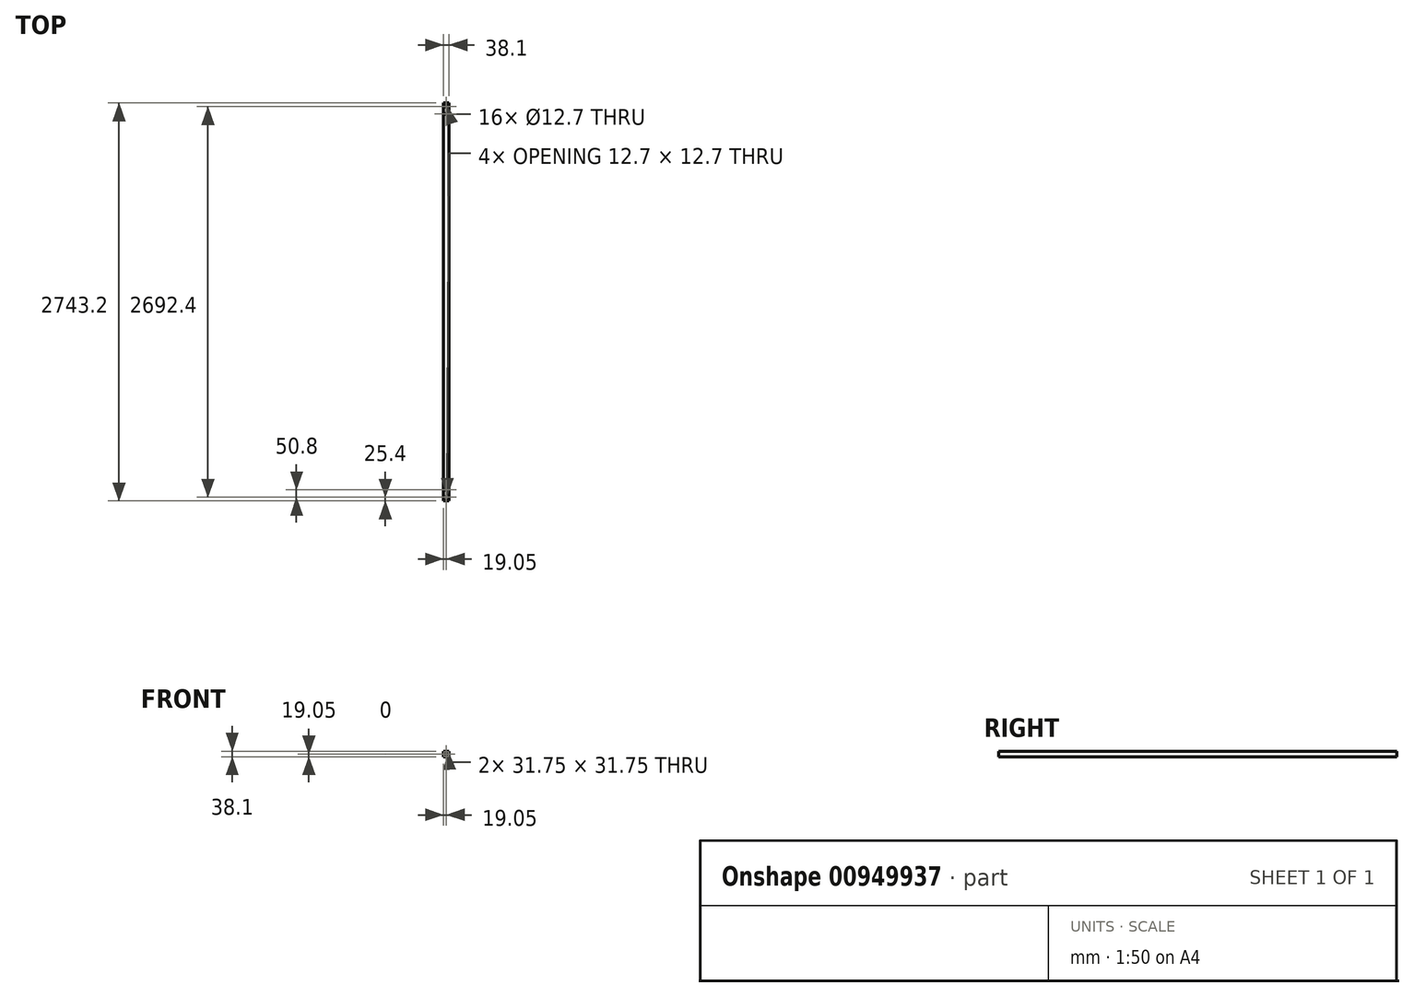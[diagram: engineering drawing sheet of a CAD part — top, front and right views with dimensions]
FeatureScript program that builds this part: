
annotation { "Feature Type Name" : "Feature", "Feature Type Description" : "" }
export const myFeature = defineFeature(function(context is Context, id is Id, definition is map)
    precondition{}
    {
        {
            var Q0;
            Q0=qCreatedBy(makeId("Front.planeOp"),FACE);
            var sketch = newSketch(context, id + "F0", { "sketchPlane" : qUnion([Q0])});
            skLineSegment(sketch, "E0.bottom", {"start": v(19.05, -19.05) * mm, "end": v(-19.05, -19.05) * mm});
            skLineSegment(sketch, "E0.top", {"start": v(19.05, 19.05) * mm, "end": v(-19.05, 19.05) * mm});
            skLineSegment(sketch, "E0.left", {"start": v(19.05, -19.05) * mm, "end": v(19.05, 19.05) * mm});
            skLineSegment(sketch, "E0.right", {"start": v(-19.05, -19.05) * mm, "end": v(-19.05, 19.05) * mm});
            skPoint(sketch, "E0.middle", {"position": v(0, 0) * mm});
            skLineSegment(sketch, "E1.bottom", {"start": v(15.88, -15.87) * mm, "end": v(-15.87, -15.88) * mm});
            skLineSegment(sketch, "E1.top", {"start": v(15.88, 15.88) * mm, "end": v(-15.88, 15.87) * mm});
            skLineSegment(sketch, "E1.left", {"start": v(15.88, -15.88) * mm, "end": v(15.88, 15.88) * mm});
            skLineSegment(sketch, "E1.right", {"start": v(-15.87, -15.88) * mm, "end": v(-15.88, 15.88) * mm});
            skSolve(sketch);
        }
        {
            var Q0;
            Q0 = qSketchRegion(id + "F0", true);
            var Q1;
            Q1 = qSketchRegion(id + "F2", true);
            extrude(context, id + "F1", {"entities" : qUnion([Q0, Q1]), "depth" : 2743.2 * mm, "offsetDistance" : 25.4 * mm});
        }
        {
            var Q0;
            Q0=makeQuery(id+"F1.opExtrude","SWEPT_FACE",FACE,{"disambiguationData":[OSD([sQuery(id+"F0.wireOp",EDGE,"E0.top")])]});
            var sketch = newSketch(context, id + "F2", { "sketchPlane" : qUnion([Q0])});
            skCircle(sketch, "E2", {"center": v(0, -25.4) * mm, "radius": 6.35 * mm});
            skCircle(sketch, "E3", {"center": v(0, -76.2) * mm, "radius": 6.35 * mm});
            skCircle(sketch, "E4", {"center": v(0, -2717.8) * mm, "radius": 6.35 * mm});
            skCircle(sketch, "E5", {"center": v(0, -2667) * mm, "radius": 6.35 * mm});
            skSolve(sketch);
        }
        {
            var Q0;
            Q0 = qSketchRegion(id + "F2", true);
            extrude(context, id + "F3", {"entities" : qUnion([Q0]), "operationType" : NewBodyOperationType.REMOVE, "endBound" : BoundingType.THROUGH_ALL, "oppositeDirection" : true, "depth" : 25.4 * mm, "offsetDistance" : 25.4 * mm});
        }
    });
